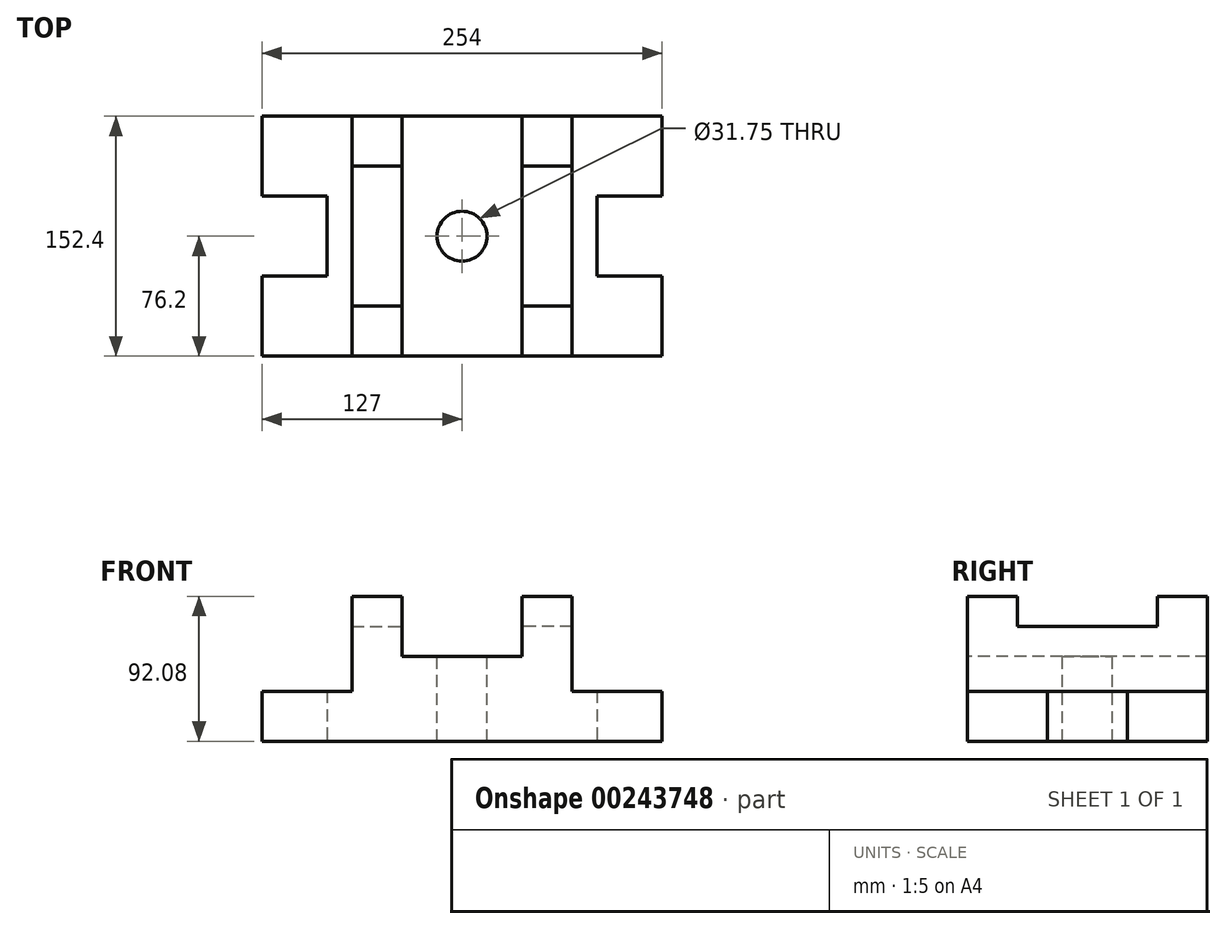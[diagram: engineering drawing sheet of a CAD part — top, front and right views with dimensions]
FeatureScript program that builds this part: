
annotation { "Feature Type Name" : "Feature", "Feature Type Description" : "" }
export const myFeature = defineFeature(function(context is Context, id is Id, definition is map)
    precondition{}
    {
        {
            var Q0;
            Q0=qCreatedBy(makeId("Top.planeOp"),FACE);
            var sketch = newSketch(context, id + "F0", { "sketchPlane" : qUnion([Q0])});
            skLineSegment(sketch, "E0.bottom", {"start": v(0, 76.2) * mm, "end": v(127, 76.2) * mm});
            skLineSegment(sketch, "E0.top", {"start": v(0, -76.2) * mm, "end": v(127, -76.2) * mm});
            skLineSegment(sketch, "E0.left", {"start": v(0, 76.2) * mm, "end": v(0, -76.2) * mm});
            skLineSegment(sketch, "E0.right", {"start": v(127, 76.2) * mm, "end": v(127, 25.4) * mm});
            skLineSegment(sketch, "E1", {"start": v(127, 25.4) * mm, "end": v(85.72, 25.4) * mm});
            skLineSegment(sketch, "E2", {"start": v(85.72, 25.4) * mm, "end": v(85.72, -25.4) * mm});
            skLineSegment(sketch, "E3", {"start": v(85.72, -25.4) * mm, "end": v(127, -25.4) * mm});
            skLineSegment(sketch, "E4.trimOffspring", {"start": v(127, -25.4) * mm, "end": v(127, -76.2) * mm});
            skLineSegment(sketch, "E5.MirrorCS", {"start": v(0, 76.2) * mm, "end": v(-127, 76.2) * mm});
            skLineSegment(sketch, "E6.MirrorCS", {"start": v(-127, 76.2) * mm, "end": v(-127, 25.4) * mm});
            skLineSegment(sketch, "E7.MirrorCS", {"start": v(-127, 25.4) * mm, "end": v(-85.72, 25.4) * mm});
            skLineSegment(sketch, "E8.MirrorCS", {"start": v(-85.72, 25.4) * mm, "end": v(-85.72, -25.4) * mm});
            skLineSegment(sketch, "E9.MirrorCS", {"start": v(-85.72, -25.4) * mm, "end": v(-127, -25.4) * mm});
            skLineSegment(sketch, "E10.MirrorCS", {"start": v(-127, -25.4) * mm, "end": v(-127, -76.2) * mm});
            skLineSegment(sketch, "E11.MirrorCS", {"start": v(0, -76.2) * mm, "end": v(-127, -76.2) * mm});
            skSolve(sketch);
        }
        {
            var Q0;
            Q0=makeQuery(id+"F0.imprint","IMPRINT",FACE,{"disambiguationData":[TD([[makeQuery(id+"F0.imprint","IMPRINT",EDGE,{"derivedFrom":sQuery(id+"F0.wireOp",EDGE,"E0.left")}),-1.0]])]});
            var Q1;
            Q1=makeQuery(id+"F0.imprint","IMPRINT",FACE,{"disambiguationData":[TD([[makeQuery(id+"F0.imprint","IMPRINT",EDGE,{"derivedFrom":sQuery(id+"F0.wireOp",EDGE,"E0.bottom")}),-1.0]])]});
            extrude(context, id + "F1", {"entities" : qUnion([Q0, Q1]), "depth" : 31.75 * mm});
        }
        {
            var Q0;
            Q0=makeQuery(id+"F1.opExtrude","CAP_FACE",FACE,{"disambiguationData":[OSD([sQuery(id+"F0.wireOp",EDGE,"E0.bottom"),sQuery(id+"F0.wireOp",EDGE,"E0.top"),sQuery(id+"F0.wireOp",EDGE,"E0.right"),sQuery(id+"F0.wireOp",EDGE,"E1"),sQuery(id+"F0.wireOp",EDGE,"E2"),sQuery(id+"F0.wireOp",EDGE,"E3"),sQuery(id+"F0.wireOp",EDGE,"E4.trimOffspring"),sQuery(id+"F0.wireOp",EDGE,"E5.MirrorCS"),sQuery(id+"F0.wireOp",EDGE,"E6.MirrorCS"),sQuery(id+"F0.wireOp",EDGE,"E7.MirrorCS"),sQuery(id+"F0.wireOp",EDGE,"E8.MirrorCS"),sQuery(id+"F0.wireOp",EDGE,"E9.MirrorCS"),sQuery(id+"F0.wireOp",EDGE,"E10.MirrorCS"),sQuery(id+"F0.wireOp",EDGE,"E11.MirrorCS")])],"isStart":false});
            var sketch = newSketch(context, id + "F2", { "sketchPlane" : qUnion([Q0])});
            skLineSegment(sketch, "E12.bottom", {"start": v(0, 76.2) * mm, "end": v(69.85, 76.2) * mm});
            skLineSegment(sketch, "E12.top", {"start": v(0, -76.2) * mm, "end": v(69.85, -76.2) * mm});
            skLineSegment(sketch, "E12.left", {"start": v(0, 76.2) * mm, "end": v(0, -76.2) * mm});
            skLineSegment(sketch, "E12.right", {"start": v(69.85, 76.2) * mm, "end": v(69.85, -76.2) * mm});
            skLineSegment(sketch, "E13.MirrorCS", {"start": v(-69.85, 76.2) * mm, "end": v(-69.85, -76.2) * mm});
            skLineSegment(sketch, "E14.MirrorCS", {"start": v(0, 76.2) * mm, "end": v(-69.85, 76.2) * mm});
            skLineSegment(sketch, "E15.MirrorCS", {"start": v(0, -76.2) * mm, "end": v(-69.85, -76.2) * mm});
            skSolve(sketch);
        }
        {
            var Q0;
            Q0 = qSketchRegion(id + "F2", true);
            extrude(context, id + "F3", {"entities" : qUnion([Q0]), "operationType" : NewBodyOperationType.ADD, "depth" : 22.22 * mm});
        }
        {
            var Q0;
            Q0=makeQuery(id+"F3.opExtrude","CAP_FACE",FACE,{"disambiguationData":[OSD([sQuery(id+"F2.wireOp",EDGE,"E12.bottom"),sQuery(id+"F2.wireOp",EDGE,"E12.top"),sQuery(id+"F2.wireOp",EDGE,"E12.right"),sQuery(id+"F2.wireOp",EDGE,"E13.MirrorCS"),sQuery(id+"F2.wireOp",EDGE,"E14.MirrorCS"),sQuery(id+"F2.wireOp",EDGE,"E15.MirrorCS")])],"isStart":false});
            var sketch = newSketch(context, id + "F4", { "sketchPlane" : qUnion([Q0])});
            skLineSegment(sketch, "E16.bottom", {"start": v(69.85, 76.2) * mm, "end": v(38.1, 76.2) * mm});
            skLineSegment(sketch, "E16.top", {"start": v(69.85, -76.2) * mm, "end": v(38.1, -76.2) * mm});
            skLineSegment(sketch, "E16.left", {"start": v(69.85, 76.2) * mm, "end": v(69.85, -76.2) * mm});
            skLineSegment(sketch, "E16.right", {"start": v(38.1, 76.2) * mm, "end": v(38.1, -76.2) * mm});
            skLineSegment(sketch, "E17.MirrorCS", {"start": v(-38.1, 76.2) * mm, "end": v(-38.1, -76.2) * mm});
            skLineSegment(sketch, "E18.MirrorCS", {"start": v(-69.85, 76.2) * mm, "end": v(-69.85, -76.2) * mm});
            skLineSegment(sketch, "E19.MirrorCS", {"start": v(-69.85, -76.2) * mm, "end": v(-38.1, -76.2) * mm});
            skLineSegment(sketch, "E20.MirrorCS", {"start": v(-69.85, 76.2) * mm, "end": v(-38.1, 76.2) * mm});
            skSolve(sketch);
        }
        {
            var Q0;
            Q0 = qSketchRegion(id + "F4", true);
            extrude(context, id + "F5", {"entities" : qUnion([Q0]), "operationType" : NewBodyOperationType.ADD, "depth" : 19.05 * mm});
        }
        {
            var Q0;
            Q0=makeQuery(id+"F3.opExtrude","CAP_FACE",FACE,{"disambiguationData":[OSD([sQuery(id+"F2.wireOp",EDGE,"E12.bottom"),sQuery(id+"F2.wireOp",EDGE,"E12.top"),sQuery(id+"F2.wireOp",EDGE,"E12.right"),sQuery(id+"F2.wireOp",EDGE,"E13.MirrorCS"),sQuery(id+"F2.wireOp",EDGE,"E14.MirrorCS"),sQuery(id+"F2.wireOp",EDGE,"E15.MirrorCS")])],"isStart":false});
            var sketch = newSketch(context, id + "F6", { "sketchPlane" : qUnion([Q0])});
            skCircle(sketch, "E21", {"center": v(0, 0) * mm, "radius": 15.88 * mm});
            skSolve(sketch);
        }
        {
            var Q0;
            Q0=sQuery(id+"F6.wireOp",VERTEX,"E21.center");
            var Q1;
            Q1=makeQuery(id+"F1.opExtrude","SWEPT_BODY",BODY,{"disambiguationData":[OSD([sQuery(id+"F0.wireOp",EDGE,"E0.bottom"),sQuery(id+"F0.wireOp",EDGE,"E0.top"),sQuery(id+"F0.wireOp",EDGE,"E0.right"),sQuery(id+"F0.wireOp",EDGE,"E1"),sQuery(id+"F0.wireOp",EDGE,"E2"),sQuery(id+"F0.wireOp",EDGE,"E3"),sQuery(id+"F0.wireOp",EDGE,"E4.trimOffspring"),sQuery(id+"F0.wireOp",EDGE,"E5.MirrorCS"),sQuery(id+"F0.wireOp",EDGE,"E6.MirrorCS"),sQuery(id+"F0.wireOp",EDGE,"E7.MirrorCS"),sQuery(id+"F0.wireOp",EDGE,"E8.MirrorCS"),sQuery(id+"F0.wireOp",EDGE,"E9.MirrorCS"),sQuery(id+"F0.wireOp",EDGE,"E10.MirrorCS"),sQuery(id+"F0.wireOp",EDGE,"E11.MirrorCS")])]});
            hole(context, id + "F7", {"style" : HoleStyle.SIMPLE, "endStyle" : HoleEndStyle.THROUGH, "holeDiameter" : 31.75 * mm, "locations" : qUnion([Q0]), "scope" : qUnion([Q1]), "isTappedThrough" : true});
        }
        {
            var Q0;
            Q0=makeQuery(id+"F5.opExtrude","CAP_FACE",FACE,{"disambiguationData":[OSD([sQuery(id+"F4.wireOp",EDGE,"E17.MirrorCS"),sQuery(id+"F4.wireOp",EDGE,"E18.MirrorCS"),sQuery(id+"F4.wireOp",EDGE,"E19.MirrorCS"),sQuery(id+"F4.wireOp",EDGE,"E20.MirrorCS")])],"isStart":false});
            var sketch = newSketch(context, id + "F8", { "sketchPlane" : qUnion([Q0])});
            skLineSegment(sketch, "E22.bottom", {"start": v(-69.85, 76.2) * mm, "end": v(-38.1, 76.2) * mm});
            skLineSegment(sketch, "E22.top", {"start": v(-69.85, 44.45) * mm, "end": v(-38.1, 44.45) * mm});
            skLineSegment(sketch, "E22.left", {"start": v(-69.85, 76.2) * mm, "end": v(-69.85, 44.45) * mm});
            skLineSegment(sketch, "E22.right", {"start": v(-38.1, 76.2) * mm, "end": v(-38.1, 44.45) * mm});
            skLineSegment(sketch, "E23.bottom", {"start": v(-69.85, -76.2) * mm, "end": v(-38.1, -76.2) * mm});
            skLineSegment(sketch, "E23.top", {"start": v(-69.85, -44.45) * mm, "end": v(-38.1, -44.45) * mm});
            skLineSegment(sketch, "E23.left", {"start": v(-69.85, -76.2) * mm, "end": v(-69.85, -44.45) * mm});
            skLineSegment(sketch, "E23.right", {"start": v(-38.1, -76.2) * mm, "end": v(-38.1, -44.45) * mm});
            skLineSegment(sketch, "E24.MirrorCS", {"start": v(69.85, 44.45) * mm, "end": v(38.1, 44.45) * mm});
            skLineSegment(sketch, "E25.MirrorCS", {"start": v(69.85, 76.2) * mm, "end": v(69.85, 44.45) * mm});
            skLineSegment(sketch, "E26.MirrorCS", {"start": v(38.1, 76.2) * mm, "end": v(38.1, 44.45) * mm});
            skLineSegment(sketch, "E27.MirrorCS", {"start": v(69.85, 76.2) * mm, "end": v(38.1, 76.2) * mm});
            skLineSegment(sketch, "E28.MirrorCS", {"start": v(69.85, -44.45) * mm, "end": v(38.1, -44.45) * mm});
            skLineSegment(sketch, "E29.MirrorCS", {"start": v(69.85, -76.2) * mm, "end": v(38.1, -76.2) * mm});
            skLineSegment(sketch, "E30.MirrorCS", {"start": v(38.1, -76.2) * mm, "end": v(38.1, -44.45) * mm});
            skLineSegment(sketch, "E31.MirrorCS", {"start": v(69.85, -76.2) * mm, "end": v(69.85, -44.45) * mm});
            skSolve(sketch);
        }
        {
            var Q0;
            Q0 = qSketchRegion(id + "F8", true);
            extrude(context, id + "F9", {"entities" : qUnion([Q0]), "operationType" : NewBodyOperationType.ADD, "depth" : 19.05 * mm});
        }
    });
